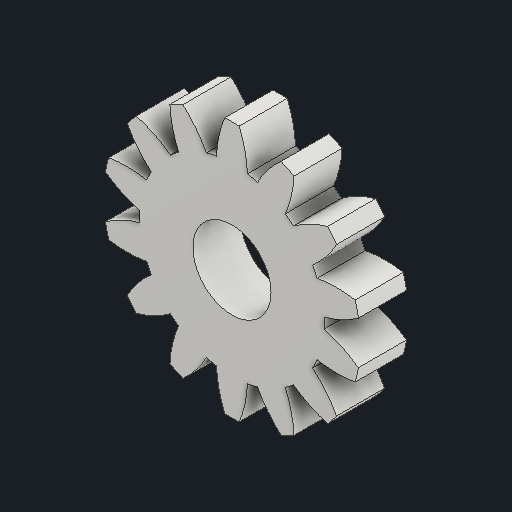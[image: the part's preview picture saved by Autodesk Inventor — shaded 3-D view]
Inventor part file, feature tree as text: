
AUTODESK INVENTOR PART (.ipt)
format: ipt  version: 2025.3 (Build 293356030, 356C)  size: 225,792 bytes
history: native  units: mm (DEFAULTED — no unit token found)
features: plane x3, other x3, extrude x2, sketch x2
ambient origin geometry x8: Origin, YZ Plane, XZ Plane, XY Plane, X Axis, Y Axis, Z Axis, Center Point
bodies: Solid1 (feature_tree)
feature tree (10):
  extrude  "Extrusion1"  Depth=3.0mm TaperAngle=0.0deg
  plane  "Work Plane2"
  plane  "Work Plane8"
  plane  "Work Plane9"
  other  "正齒輪"
  extrude  "擠出2"  Depth=10.0mm
  sketch  "Sketch1"  dims[d0=16.0mm d1=3.0mm d2=0.0mm d3=14.0mm d4=10.0mm d5=0.0mm d16=17.5mm d17=0.0mm d34=2.243995mm d39=0.0mm d41=0.0mm d43=17.5mm d46=17.5mm d47=0.0mm d48=0.0mm d49=4.88mm d50=10.0mm d51=0.0mm]
  other  "Srf1"
  sketch  "草圖3"
  other  "節圓直徑"
